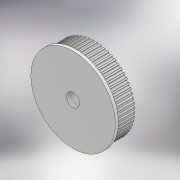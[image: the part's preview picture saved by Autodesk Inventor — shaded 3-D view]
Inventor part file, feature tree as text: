
AUTODESK INVENTOR PART (.ipt)
format: ipt  version: 2018.2 (Build 222227000, 227)  size: 437,248 bytes
history: native  units: mm
features: extrude x6, sketch x5, pattern_circular x1
ambient origin geometry x8: Origin, YZ Plane, XZ Plane, XY Plane, X Axis, Y Axis, Z Axis, Center Point
bodies: Solid1 (feature_tree)
feature tree (12):
  extrude  "Extrusion1"  Depth=0.5mm
  extrude  "Extrusion2"  Depth=7.0mm TaperAngle=0.0deg
  pattern_circular  "Circular Pattern1"  [2 undecoded]
  extrude  "Extrusion3"  Depth=1.0mm TaperAngle=0.0deg
  sketch  "Sketch4"  dims[d18=6.35mm]
  extrude  "Extrusion4"  Depth=6.0mm TaperAngle=0.0deg
  extrude  "Extrusion5"  Depth=3.0mm
  extrude  "Extrusion6"  Depth=6.0mm TaperAngle=0.0deg
  sketch  "Sketch1"  dims[d8=0.0mm d9=0.5mm]
  sketch  "Sketch2"  dims[d10=0.15mm d12=7.0mm d13=0.0mm]
  sketch  "Sketch3"  dims[d15=360.0deg]
  sketch  "Sketch5"  dims[d20=0.0mm d21=2.0mm d22=1.0mm d23=0.0mm d24=6.0mm d25=0.0mm d26=3.0mm d27=6.0mm d28=0.0mm]
note: 2 required parameter values undecoded (feature->parameter linkage not recoverable at this tier; creation-order binding heuristic only, values carry confidence <= 0.55)
